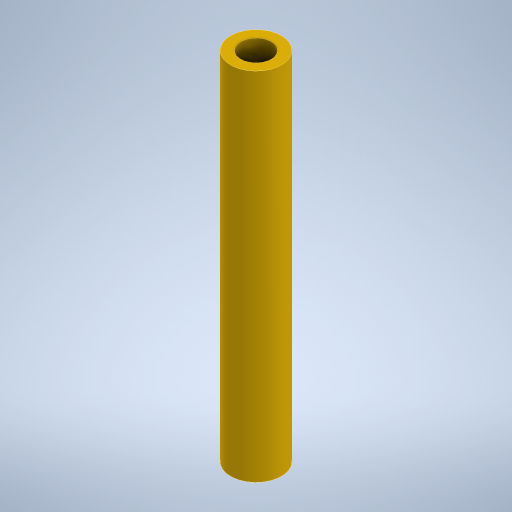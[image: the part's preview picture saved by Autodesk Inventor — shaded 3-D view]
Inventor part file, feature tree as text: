
AUTODESK INVENTOR PART (.ipt)
format: ipt  version: 2023 (Build 270158000, 158)  size: 225,792 bytes
history: native  units: in
note: dims shown in document units (in); Inventor stores cm internally (conversion verified against a paired STEP export)
features: extrude x1, sketch x1
ambient origin geometry x8: Origin, YZ Plane, XZ Plane, XY Plane, X Axis, Y Axis, Z Axis, Center Point
bodies: Solid1 (feature_tree)
feature tree (2):
  extrude  "Extrusion1"  Depth=1.378in
  sketch  "Sketch1"  dims[d0=0.1969in d1=0.1181in d2=1.378in d3=0.0in]
